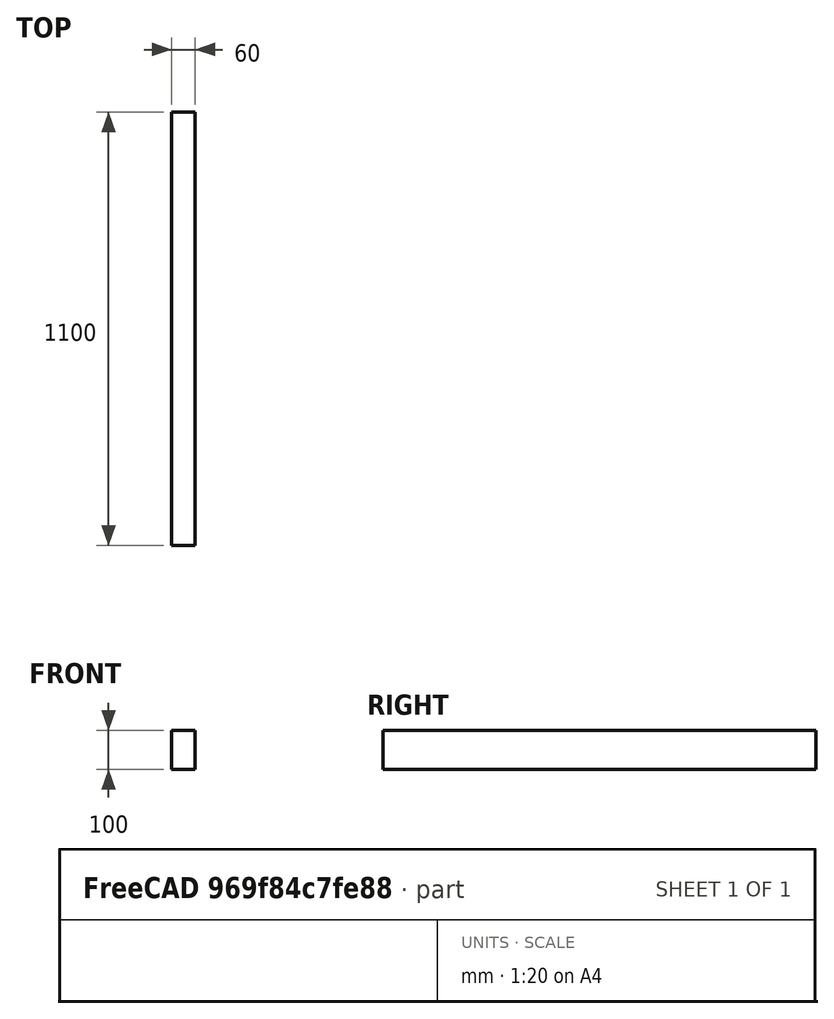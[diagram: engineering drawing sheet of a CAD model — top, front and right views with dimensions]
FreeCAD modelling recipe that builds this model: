
FCSTD DOCUMENT  (FreeCAD 1.0RUnknown)
Label: beam60x100x980
License: All rights reserved
LicenseURL: https://en.wikipedia.org/wiki/All_rights_reserved
objects: PartDesign::CoordinateSystem×3, Sketcher::SketchObject×1, PartDesign::Pad×1, PartDesign::Body×1, App::Part×1
note: 9 computed .brp shape members not serialized (recipe doc carries the construction recipe); baked Part::Feature solids carry a one-line shape summary decoded from their .brp

FEATURE [Sketcher::SketchObject] Sketch
  ArcFitTolerance = 1e-06
  AttachmentSupport = -> [XZ_Plane]
  FullyConstrained = true
  MakeInternals = false
  MapMode = 5
  Placement = pos=(0,0,0) rot=(1,0,0;1.5708rad)
  sketch-geometry (5):
    g0: LineSegment StartX=-30 StartY=-50 StartZ=0 EndX=30 EndY=-50 EndZ=0
    g1: LineSegment StartX=30 StartY=-50 StartZ=0 EndX=30 EndY=50 EndZ=0
    g2: LineSegment StartX=30 StartY=50 StartZ=0 EndX=-30 EndY=50 EndZ=0
    g3: LineSegment StartX=-30 StartY=50 StartZ=0 EndX=-30 EndY=-50 EndZ=0
    g4: GeomPoint [constr] X=0 Y=0 Z=0
  constraints (12):
    c: Coincident(g0,g1)
    c: Coincident(g1,g2)
    c: Coincident(g2,g3)
    c: Coincident(g3,g0)
    c: Horizontal(g0)
    c: Horizontal(g2)
    c: Vertical(g1)
    c: Vertical(g3)
    c: Symmetric(g2,g0,g4)
    c: Coincident(g4,g-1)
    c: DistanceX(g0,g0) = 60
    c: DistanceY(g3,g3) = 100
FEATURE [PartDesign::Pad] Pad
  Direction = (0,-1,2e-16)
  Length = 1100
  Length2 = 10
  Midplane = true
  Placement = pos=(0,0,0) rot=(1,0,0;1.5708rad)
  Profile = -> Sketch
  ReferenceAxis = -> Sketch [N_Axis]
  Refine = true
  Suppressed = false
  Type = 0
FEATURE [PartDesign::Body] Body  label="Körper"
  AllowCompound = false
  Group = -> [Sketch,Pad]
  Origin = -> Origin
  Tip = -> Pad
FEATURE [PartDesign::CoordinateSystem] LCS_Origin
  AttacherType = Attacher::AttachEngine3D
  AttachmentSupport = -> [X_Axis001]
  MapMode = 2
FEATURE [PartDesign::CoordinateSystem] LCS_1
  AttacherType = Attacher::AttachEngine3D
  AttachmentSupport = -> [Pad]
  MapMode = 45
  Placement = pos=(-30,550,-1.221e-13) rot=(0,0,1;0rad)
FEATURE [PartDesign::CoordinateSystem] LCS_2
  AttacherType = Attacher::AttachEngine3D
  AttachmentSupport = -> [Pad]
  MapMode = 45
  Placement = pos=(-30,-550,1.221e-13) rot=(0,0,1;0rad)
FEATURE [App::Part] beam60x100x887  label="beam60x100x800"
  Group = -> [LCS_Origin,Body,LCS_1,LCS_2]
  Origin = -> Origin001
